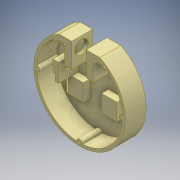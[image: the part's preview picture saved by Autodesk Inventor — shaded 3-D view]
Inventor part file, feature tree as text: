
AUTODESK INVENTOR PART (.ipt)
format: ipt  version: 2016 (Build 200138000, 138)  size: 319,488 bytes
history: native  units: mm
features: extrude x12, sketch x12, other x1
ambient origin geometry x8: Origin, YZ Plane, XZ Plane, XY Plane, X Axis, Y Axis, Z Axis, Center Point
bodies: Body1 (feature_tree)
feature tree (25):
  other  "Sólido1"
  extrude  "Extrusión1"  Depth=18.0mm
  extrude  "Extrusión2"  Depth=15.0mm
  extrude  "Extrusión3"  Depth=15.0mm
  extrude  "Extrusión4"  Depth=40.0mm
  extrude  "Extrusión5"  Depth=2.0mm TaperAngle=0.0deg
  extrude  "Extrusión6"  Depth=140.0mm
  extrude  "Extrusión8"  Depth=25.0mm
  extrude  "Extrusión9"  Depth=25.0mm
  extrude  "Extrusión10"  Depth=11.0mm TaperAngle=0.0deg
  extrude  "Extrusión11"  Depth=32.0mm TaperAngle=0.0deg
  extrude  "Extrusión12"  Depth=21.0mm
  extrude  "Extrusión13"  Depth=38.0mm TaperAngle=0.0deg
  sketch  "Boceto1"  dims[d0=150.0mm d2=18.0mm]
  sketch  "Boceto2"  dims[d3=25.0mm d4=15.0mm]
  sketch  "Boceto3"  dims[d5=50.0mm d6=15.0mm]
  sketch  "Boceto4"  dims[d7=50.0mm d8=40.0mm]
  sketch  "Boceto5"  dims[d9=40.0mm d12=2.0mm d13=0.0mm]
  sketch  "Boceto6"  dims[d14=150.0mm d23=140.0mm]
  sketch  "Boceto8"  dims[d25=32.0mm d26=0.0mm d27=25.0mm]
  sketch  "Boceto9"  dims[d28=28.0mm d30=25.0mm]
  sketch  "Boceto10"  dims[d31=28.0mm d33=11.0mm d34=0.0mm]
  sketch  "Boceto11"  dims[d37=21.0mm d38=32.0mm d39=0.0mm]
  sketch  "Boceto12"  dims[d40=22.0mm d41=21.0mm]
  sketch  "Boceto13"  dims[d42=18.0mm d43=38.0mm d44=0.0mm d45=10.0mm d46=10.0mm d47=10.0mm d48=3.0mm d49=3.0mm d50=3.0mm d51=33.0mm d52=0.0mm d63=8.0mm d64=8.0mm d65=11.0mm d66=11.0mm d67=15.0mm d69=70.0mm d70=0.0mm d71=5.0mm d72=140.0mm d73=12.0mm d76=10.0mm d77=12.0mm d78=10.0mm d79=32.0mm d80=0.0mm d81=8.0mm d82=8.0mm d83=8.0mm d84=8.0mm d85=32.0mm d86=0.0mm d89=3.0mm d90=3.0mm d91=3.0mm d92=3.0mm d93=32.0mm d94=0.0mm d95=8.0mm d96=16.0mm d97=15.0mm d98=3.0mm d99=5.0mm d102=3.0mm d103=5.0mm d104=3.0mm d105=5.0mm d106=3.0mm d107=16.0mm d108=16.0mm d109=15.0mm d110=23.5mm d111=50.0mm d112=0.0mm d116=32.0mm d117=0.0mm]
